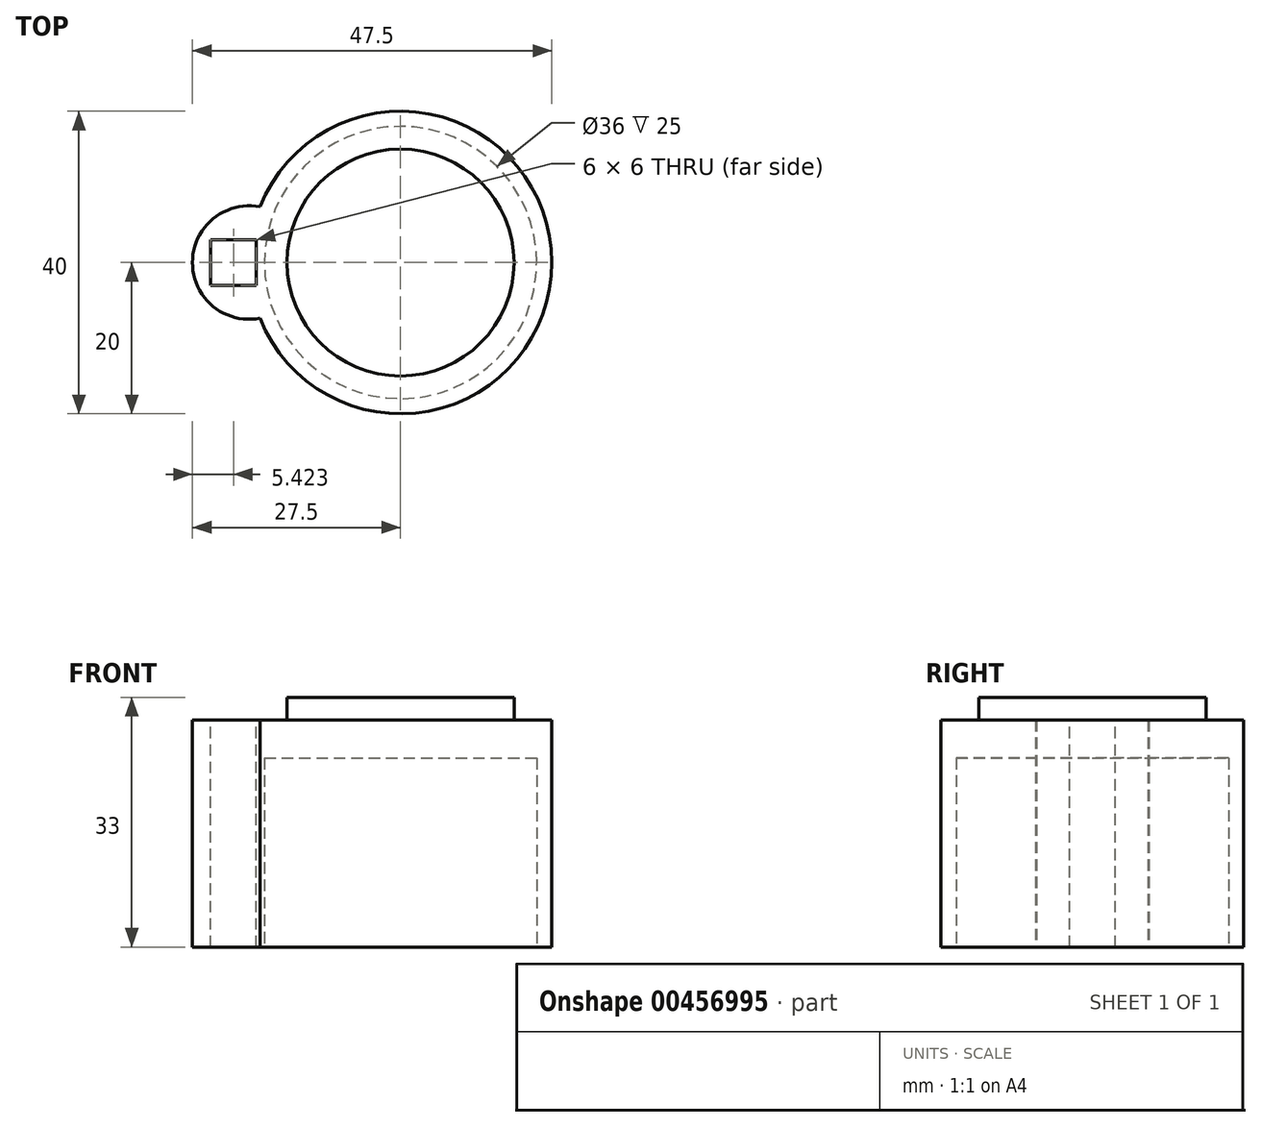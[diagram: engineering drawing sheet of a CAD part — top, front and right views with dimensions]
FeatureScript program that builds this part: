
annotation { "Feature Type Name" : "Feature", "Feature Type Description" : "" }
export const myFeature = defineFeature(function(context is Context, id is Id, definition is map)
    precondition{}
    {
        {
            var Q0;
            Q0=qCreatedBy(makeId("Top.planeOp"),FACE);
            var sketch = newSketch(context, id + "F0", { "sketchPlane" : qUnion([Q0])});
            skCircle(sketch, "E0", {"center": v(0, 0) * mm, "radius": 20 * mm});
            skCircle(sketch, "E1", {"center": v(0, 0) * mm, "radius": 15 * mm});
            skArc(sketch, "E2", {"start": v(-18.6, 7.37) * mm, "mid": v(-27.5, 0) * mm, "end": v(-18.6, -7.37) * mm});
            skSolve(sketch);
        }
        {
            var Q0;
            Q0 = qSketchRegion(id + "F0", true);
            var Q1;
            Q1=makeQuery(id+"F0.imprint","IMPRINT",FACE,{"disambiguationData":[TD([[makeQuery(id+"F0.imprint","IMPRINT",EDGE,{"derivedFrom":sQuery(id+"F0.wireOp",EDGE,"E1")}),1.0]])]});
            extrude(context, id + "F1", {"entities" : qUnion([Q0, Q1]), "depth" : 30 * mm});
        }
        {
            var Q0;
            Q0=makeQuery(id+"F1.opExtrude","CAP_FACE",FACE,{"disambiguationData":[OSD([sQuery(id+"F0.wireOp",EDGE,"E0"),sQuery(id+"F0.wireOp",EDGE,"E2")])],"isStart":false});
            var sketch = newSketch(context, id + "F2", { "sketchPlane" : qUnion([Q0])});
            skLineSegment(sketch, "E3.bottom", {"start": v(-19.08, -3) * mm, "end": v(-25.08, -3) * mm});
            skLineSegment(sketch, "E3.top", {"start": v(-19.08, 3) * mm, "end": v(-25.08, 3) * mm});
            skLineSegment(sketch, "E3.left", {"start": v(-19.08, -3) * mm, "end": v(-19.08, 3) * mm});
            skLineSegment(sketch, "E3.right", {"start": v(-25.08, -3) * mm, "end": v(-25.08, 3) * mm});
            skPoint(sketch, "E3.middle", {"position": v(-22.08, 0) * mm});
            skSolve(sketch);
        }
        {
            var Q0;
            Q0=makeQuery(id+"F1.opExtrude","CAP_FACE",FACE,{"disambiguationData":[OSD([sQuery(id+"F0.wireOp",EDGE,"E0"),sQuery(id+"F0.wireOp",EDGE,"E2")])],"isStart":true});
            var sketch = newSketch(context, id + "F3", { "sketchPlane" : qUnion([Q0])});
            skCircle(sketch, "E4", {"center": v(0, 0) * mm, "radius": 18 * mm});
            skSolve(sketch);
        }
        {
            var Q0;
            Q0=makeQuery(id+"F3.imprint","IMPRINT",FACE,{"disambiguationData":[TD([[makeQuery(id+"F3.imprint","IMPRINT",EDGE,{"derivedFrom":sQuery(id+"F3.wireOp",EDGE,"E4")}),1.0]])]});
            var Q1;
            Q1 = qSketchRegion(id + "F3", true);
            extrude(context, id + "F4", {"entities" : qUnion([Q0, Q1]), "operationType" : NewBodyOperationType.REMOVE, "oppositeDirection" : true, "depth" : 25 * mm});
        }
        {
            var Q0;
            Q0=makeQuery(id+"F2.imprint","IMPRINT",FACE,{"disambiguationData":[TD([[makeQuery(id+"F2.imprint","IMPRINT",EDGE,{"derivedFrom":sQuery(id+"F2.wireOp",EDGE,"E3.bottom")}),1.0]])]});
            var sketch = newSketch(context, id + "F5", { "sketchPlane" : qUnion([Q0])});
            skCircle(sketch, "E5", {"center": v(0, 0) * mm, "radius": 15 * mm});
            skSolve(sketch);
        }
        {
            var Q0;
            Q0=makeQuery(id+"F5.imprint","IMPRINT",FACE,{"disambiguationData":[TD([[makeQuery(id+"F5.imprint","IMPRINT",EDGE,{"derivedFrom":sQuery(id+"F5.wireOp",EDGE,"E5")}),1.0]])]});
            extrude(context, id + "F6", {"entities" : qUnion([Q0]), "operationType" : NewBodyOperationType.ADD, "depth" : 3 * mm});
        }
        {
            var Q0;
            Q0=makeQuery(id+"F2.imprint","IMPRINT",FACE,{"disambiguationData":[TD([[makeQuery(id+"F2.imprint","IMPRINT",EDGE,{"derivedFrom":sQuery(id+"F2.wireOp",EDGE,"E3.bottom")}),-1.0]])]});
            extrude(context, id + "F7", {"entities" : qUnion([Q0]), "operationType" : NewBodyOperationType.REMOVE, "oppositeDirection" : true, "depth" : 35 * mm});
        }
    });
